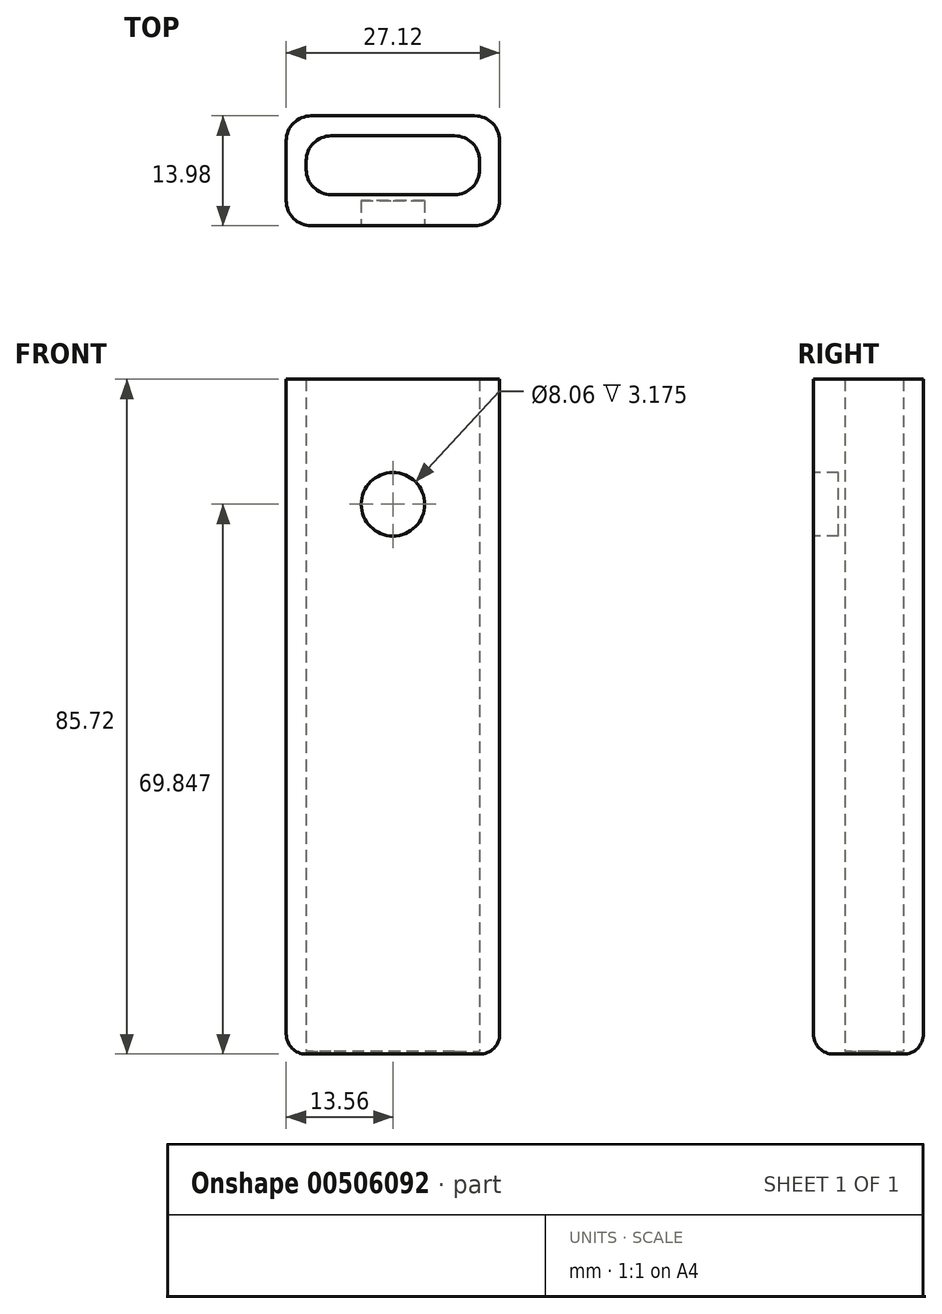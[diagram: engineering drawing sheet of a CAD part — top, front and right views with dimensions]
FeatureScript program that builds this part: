
annotation { "Feature Type Name" : "Feature", "Feature Type Description" : "" }
export const myFeature = defineFeature(function(context is Context, id is Id, definition is map)
    precondition{}
    {
        {
            var Q0;
            Q0=qCreatedBy(makeId("Top.planeOp"),FACE);
            var sketch = newSketch(context, id + "F0", { "sketchPlane" : qUnion([Q0])});
            skLineSegment(sketch, "E0.bottom", {"start": v(13.56, 6.99) * mm, "end": v(-13.56, 6.99) * mm});
            skLineSegment(sketch, "E0.top", {"start": v(13.56, -6.99) * mm, "end": v(-13.56, -6.99) * mm});
            skLineSegment(sketch, "E0.left", {"start": v(13.56, 6.99) * mm, "end": v(13.56, -6.99) * mm});
            skLineSegment(sketch, "E0.right", {"start": v(-13.56, 6.99) * mm, "end": v(-13.56, -6.99) * mm});
            skPoint(sketch, "E0.middle", {"position": v(0, 0) * mm});
            skLineSegment(sketch, "E1.0", {"start": v(11.02, 4.45) * mm, "end": v(-11.02, 4.45) * mm});
            skLineSegment(sketch, "E1.1", {"start": v(11.02, 4.45) * mm, "end": v(11.02, -3.02) * mm});
            skLineSegment(sketch, "E1.3", {"start": v(-11.02, 4.45) * mm, "end": v(-11.02, -3.02) * mm});
            skLineSegment(sketch, "E2", {"start": v(11.02, -3.02) * mm, "end": v(-11.02, -3.02) * mm});
            skSolve(sketch);
        }
        {
            var Q0;
            Q0 = qSketchRegion(id + "F0", true);
            extrude(context, id + "F1", {"entities" : qUnion([Q0]), "endBound" : BoundingType.SYMMETRIC, "depth" : 85.72 * mm});
        }
        {
            var Q0;
            Q0=makeQuery(id+"F1.opExtrude","SWEPT_EDGE",EDGE,{"disambiguationData":[OSD([sQuery(id+"F0.wireOp",EDGE,"E0.top"),sQuery(id+"F0.wireOp",EDGE,"E0.left")])]});
            var Q1;
            Q1=makeQuery(id+"F1.opExtrude","SWEPT_EDGE",EDGE,{"disambiguationData":[OSD([sQuery(id+"F0.wireOp",EDGE,"E0.top"),sQuery(id+"F0.wireOp",EDGE,"E0.right")])]});
            var Q2;
            Q2=makeQuery(id+"F1.opExtrude","SWEPT_EDGE",EDGE,{"disambiguationData":[OSD([sQuery(id+"F0.wireOp",EDGE,"E0.bottom"),sQuery(id+"F0.wireOp",EDGE,"E0.right")])]});
            var Q3;
            Q3=makeQuery(id+"F1.opExtrude","SWEPT_EDGE",EDGE,{"disambiguationData":[OSD([sQuery(id+"F0.wireOp",EDGE,"E0.bottom"),sQuery(id+"F0.wireOp",EDGE,"E0.left")])]});
            var Q4;
            Q4=makeQuery(id+"F1.opExtrude","SWEPT_EDGE",EDGE,{"disambiguationData":[OSD([sQuery(id+"F0.wireOp",EDGE,"E1.0"),sQuery(id+"F0.wireOp",EDGE,"E1.3")])]});
            var Q5;
            Q5=makeQuery(id+"F1.opExtrude","SWEPT_EDGE",EDGE,{"disambiguationData":[OSD([sQuery(id+"F0.wireOp",EDGE,"E1.0"),sQuery(id+"F0.wireOp",EDGE,"E1.1")])]});
            var Q6;
            Q6=makeQuery(id+"F1.opExtrude","SWEPT_EDGE",EDGE,{"disambiguationData":[OSD([sQuery(id+"F0.wireOp",EDGE,"E1.2"),sQuery(id+"F0.wireOp",EDGE,"E1.3")])]});
            var Q7;
            Q7=makeQuery(id+"F1.opExtrude","SWEPT_EDGE",EDGE,{"disambiguationData":[OSD([sQuery(id+"F0.wireOp",EDGE,"E1.1"),sQuery(id+"F0.wireOp",EDGE,"E1.2")])]});
            fillet(context, id + "F2", {"entities" : qUnion([Q0, Q1, Q2, Q3, Q4, Q5, Q6, Q7]), "radius" : 3.17 * mm, "tangentPropagation" : true, "allowEdgeOverflow" : false});
        }
        {
            var Q0;
            Q0=makeQuery(id+"F1.opExtrude","SWEPT_FACE",FACE,{"disambiguationData":[OSD([sQuery(id+"F0.wireOp",EDGE,"E0.top")])]});
            var sketch = newSketch(context, id + "F3", { "sketchPlane" : qUnion([Q0])});
            skCircle(sketch, "E3", {"center": v(0, 26.99) * mm, "radius": 4.03 * mm});
            skSolve(sketch);
        }
        {
            var Q0;
            Q0=makeQuery(id+"F3.imprint","IMPRINT",FACE,{"disambiguationData":[TD([[makeQuery(id+"F3.imprint","IMPRINT",EDGE,{"derivedFrom":sQuery(id+"F3.wireOp",EDGE,"E3")}),1.0]])]});
            extrude(context, id + "F4", {"entities" : qUnion([Q0]), "operationType" : NewBodyOperationType.REMOVE, "oppositeDirection" : true, "depth" : 3.17 * mm});
        }
        {
            var Q0;
            Q0=makeQuery(id+"F1.opExtrude","CAP_FACE",FACE,{"disambiguationData":[OSD([sQuery(id+"F0.wireOp",EDGE,"E0.bottom"),sQuery(id+"F0.wireOp",EDGE,"E0.top"),sQuery(id+"F0.wireOp",EDGE,"E0.left"),sQuery(id+"F0.wireOp",EDGE,"E0.right"),sQuery(id+"F0.wireOp",EDGE,"E1.0"),sQuery(id+"F0.wireOp",EDGE,"E1.1"),sQuery(id+"F0.wireOp",EDGE,"E1.3"),sQuery(id+"F0.wireOp",EDGE,"E2")])],"isStart":true});
            var sketch = newSketch(context, id + "F5", { "sketchPlane" : qUnion([Q0])});
            skArc(sketch, "E4.0", {"start": v(7.84, 3.02) * mm, "mid": v(10.09, 2.09) * mm, "end": v(11.02, -0.16) * mm});
            skArc(sketch, "E4.1", {"start": v(11.02, -1.27) * mm, "mid": v(10.09, -3.52) * mm, "end": v(7.84, -4.45) * mm});
            skLineSegment(sketch, "E4.2", {"start": v(11.02, -1.27) * mm, "end": v(11.02, -0.16) * mm});
            skLineSegment(sketch, "E4.3", {"start": v(7.84, 3.02) * mm, "end": v(-7.84, 3.02) * mm});
            skLineSegment(sketch, "E4.4", {"start": v(7.84, -4.45) * mm, "end": v(-7.84, -4.45) * mm});
            skArc(sketch, "E4.5", {"start": v(-7.84, -4.45) * mm, "mid": v(-10.09, -3.52) * mm, "end": v(-11.02, -1.27) * mm});
            skArc(sketch, "E4.6", {"start": v(-11.02, -0.16) * mm, "mid": v(-10.09, 2.09) * mm, "end": v(-7.84, 3.02) * mm});
            skLineSegment(sketch, "E4.7", {"start": v(-11.02, -1.27) * mm, "end": v(-11.02, -0.16) * mm});
            skSolve(sketch);
        }
        {
            var Q0;
            Q0 = qSketchRegion(id + "F5", true);
            extrude(context, id + "F6", {"entities" : qUnion([Q0]), "operationType" : NewBodyOperationType.ADD, "oppositeDirection" : true, "depth" : 0.32 * mm});
        }
        {
            var Q0;
            Q0=makeQuery(id+"F1.opExtrude","CAP_EDGE",EDGE,{"disambiguationData":[OSD([sQuery(id+"F0.wireOp",EDGE,"E0.top")])],"isStart":true});
            var Q1;
            {var subQ0=sQuery(id+"F0.wireOp",EDGE,"E0.left");var subQ1=sQuery(id+"F0.wireOp",EDGE,"E0.top");Q1=makeQuery(id+"F2.opFillet","BLEND_EDGE",EDGE,{"blendedFrom":[makeQuery(id+"F1.opExtrude","SWEPT_EDGE",EDGE,{"disambiguationData":[OSD([subQ1,subQ0])]}),makeQuery(id+"F1.opExtrude","CAP_FACE",FACE,{"disambiguationData":[OSD([sQuery(id+"F0.wireOp",EDGE,"E0.bottom"),subQ1,subQ0,sQuery(id+"F0.wireOp",EDGE,"E0.right"),sQuery(id+"F0.wireOp",EDGE,"E1.0"),sQuery(id+"F0.wireOp",EDGE,"E1.1"),sQuery(id+"F0.wireOp",EDGE,"E1.3"),sQuery(id+"F0.wireOp",EDGE,"E2")])],"isStart":true})],"blendedInto":[makeQuery(id+"F1.opExtrude","CAP_FACE",FACE,{"disambiguationData":[OSD([sQuery(id+"F0.wireOp",EDGE,"E0.bottom"),subQ1,subQ0,sQuery(id+"F0.wireOp",EDGE,"E0.right"),sQuery(id+"F0.wireOp",EDGE,"E1.0"),sQuery(id+"F0.wireOp",EDGE,"E1.1"),sQuery(id+"F0.wireOp",EDGE,"E1.3"),sQuery(id+"F0.wireOp",EDGE,"E2")])],"isStart":true})]});}
            var Q2;
            Q2=makeQuery(id+"F1.opExtrude","CAP_EDGE",EDGE,{"disambiguationData":[OSD([sQuery(id+"F0.wireOp",EDGE,"E0.left")])],"isStart":true});
            var Q3;
            {var subQ0=sQuery(id+"F0.wireOp",EDGE,"E0.left");var subQ1=sQuery(id+"F0.wireOp",EDGE,"E0.bottom");Q3=makeQuery(id+"F2.opFillet","BLEND_EDGE",EDGE,{"blendedFrom":[makeQuery(id+"F1.opExtrude","SWEPT_EDGE",EDGE,{"disambiguationData":[OSD([subQ1,subQ0])]}),makeQuery(id+"F1.opExtrude","CAP_FACE",FACE,{"disambiguationData":[OSD([subQ1,sQuery(id+"F0.wireOp",EDGE,"E0.top"),subQ0,sQuery(id+"F0.wireOp",EDGE,"E0.right"),sQuery(id+"F0.wireOp",EDGE,"E1.0"),sQuery(id+"F0.wireOp",EDGE,"E1.1"),sQuery(id+"F0.wireOp",EDGE,"E1.3"),sQuery(id+"F0.wireOp",EDGE,"E2")])],"isStart":true})],"blendedInto":[makeQuery(id+"F1.opExtrude","CAP_FACE",FACE,{"disambiguationData":[OSD([subQ1,sQuery(id+"F0.wireOp",EDGE,"E0.top"),subQ0,sQuery(id+"F0.wireOp",EDGE,"E0.right"),sQuery(id+"F0.wireOp",EDGE,"E1.0"),sQuery(id+"F0.wireOp",EDGE,"E1.1"),sQuery(id+"F0.wireOp",EDGE,"E1.3"),sQuery(id+"F0.wireOp",EDGE,"E2")])],"isStart":true})]});}
            var Q4;
            Q4=makeQuery(id+"F1.opExtrude","CAP_EDGE",EDGE,{"disambiguationData":[OSD([sQuery(id+"F0.wireOp",EDGE,"E0.bottom")])],"isStart":true});
            var Q5;
            {var subQ0=sQuery(id+"F0.wireOp",EDGE,"E0.right");var subQ1=sQuery(id+"F0.wireOp",EDGE,"E0.bottom");Q5=makeQuery(id+"F2.opFillet","BLEND_EDGE",EDGE,{"blendedFrom":[makeQuery(id+"F1.opExtrude","SWEPT_EDGE",EDGE,{"disambiguationData":[OSD([subQ1,subQ0])]}),makeQuery(id+"F1.opExtrude","CAP_FACE",FACE,{"disambiguationData":[OSD([subQ1,sQuery(id+"F0.wireOp",EDGE,"E0.top"),sQuery(id+"F0.wireOp",EDGE,"E0.left"),subQ0,sQuery(id+"F0.wireOp",EDGE,"E1.0"),sQuery(id+"F0.wireOp",EDGE,"E1.1"),sQuery(id+"F0.wireOp",EDGE,"E1.3"),sQuery(id+"F0.wireOp",EDGE,"E2")])],"isStart":true})],"blendedInto":[makeQuery(id+"F1.opExtrude","CAP_FACE",FACE,{"disambiguationData":[OSD([subQ1,sQuery(id+"F0.wireOp",EDGE,"E0.top"),sQuery(id+"F0.wireOp",EDGE,"E0.left"),subQ0,sQuery(id+"F0.wireOp",EDGE,"E1.0"),sQuery(id+"F0.wireOp",EDGE,"E1.1"),sQuery(id+"F0.wireOp",EDGE,"E1.3"),sQuery(id+"F0.wireOp",EDGE,"E2")])],"isStart":true})]});}
            var Q6;
            Q6=makeQuery(id+"F1.opExtrude","CAP_EDGE",EDGE,{"disambiguationData":[OSD([sQuery(id+"F0.wireOp",EDGE,"E0.right")])],"isStart":true});
            var Q7;
            {var subQ0=sQuery(id+"F0.wireOp",EDGE,"E0.right");var subQ1=sQuery(id+"F0.wireOp",EDGE,"E0.top");Q7=makeQuery(id+"F2.opFillet","BLEND_EDGE",EDGE,{"blendedFrom":[makeQuery(id+"F1.opExtrude","SWEPT_EDGE",EDGE,{"disambiguationData":[OSD([subQ1,subQ0])]}),makeQuery(id+"F1.opExtrude","CAP_FACE",FACE,{"disambiguationData":[OSD([sQuery(id+"F0.wireOp",EDGE,"E0.bottom"),subQ1,sQuery(id+"F0.wireOp",EDGE,"E0.left"),subQ0,sQuery(id+"F0.wireOp",EDGE,"E1.0"),sQuery(id+"F0.wireOp",EDGE,"E1.1"),sQuery(id+"F0.wireOp",EDGE,"E1.3"),sQuery(id+"F0.wireOp",EDGE,"E2")])],"isStart":true})],"blendedInto":[makeQuery(id+"F1.opExtrude","CAP_FACE",FACE,{"disambiguationData":[OSD([sQuery(id+"F0.wireOp",EDGE,"E0.bottom"),subQ1,sQuery(id+"F0.wireOp",EDGE,"E0.left"),subQ0,sQuery(id+"F0.wireOp",EDGE,"E1.0"),sQuery(id+"F0.wireOp",EDGE,"E1.1"),sQuery(id+"F0.wireOp",EDGE,"E1.3"),sQuery(id+"F0.wireOp",EDGE,"E2")])],"isStart":true})]});}
            fillet(context, id + "F7", {"entities" : qUnion([Q0, Q1, Q2, Q3, Q4, Q5, Q6, Q7]), "radius" : 2.54 * mm, "tangentPropagation" : true, "allowEdgeOverflow" : false});
        }
    });
